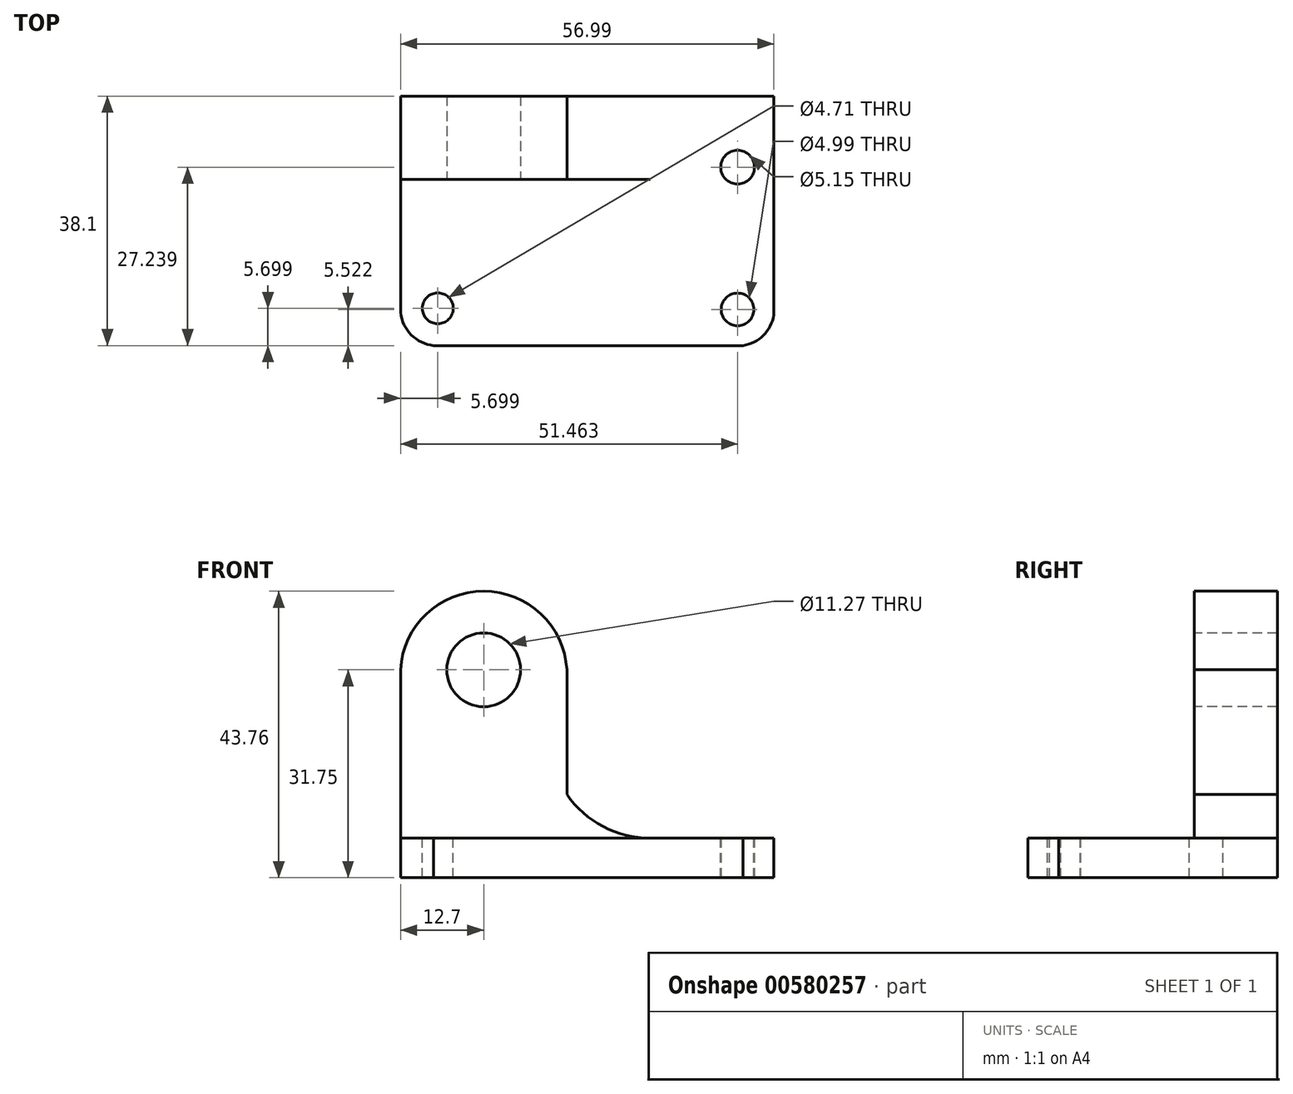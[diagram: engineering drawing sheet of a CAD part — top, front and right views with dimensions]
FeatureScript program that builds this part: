
annotation { "Feature Type Name" : "Feature", "Feature Type Description" : "" }
export const myFeature = defineFeature(function(context is Context, id is Id, definition is map)
    precondition{}
    {
        {
            var Q0;
            Q0=qCreatedBy(makeId("Front.planeOp"),FACE);
            var sketch = newSketch(context, id + "F0", { "sketchPlane" : qUnion([Q0])});
            skLineSegment(sketch, "E0", {"start": v(0, 0) * mm, "end": v(0, 6.04) * mm});
            skLineSegment(sketch, "E1", {"start": v(0, 6.04) * mm, "end": v(56.99, 6.04) * mm});
            skLineSegment(sketch, "E2", {"start": v(56.99, 6.04) * mm, "end": v(56.99, 0) * mm});
            skLineSegment(sketch, "E3", {"start": v(56.99, 0) * mm, "end": v(0, 0) * mm});
            skSolve(sketch);
        }
        {
            var Q0;
            Q0=makeQuery(id+"F0.imprint","IMPRINT",FACE,{"disambiguationData":[TD([[makeQuery(id+"F0.imprint","IMPRINT",EDGE,{"derivedFrom":sQuery(id+"F0.wireOp",EDGE,"E0")}),-1.0]])]});
            extrude(context, id + "F1", {"entities" : qUnion([Q0]), "depth" : 38.1 * mm, "offsetDistance" : 25.4 * mm});
        }
        {
            var Q0;
            Q0=qCreatedBy(makeId("Front.planeOp"),FACE);
            var sketch = newSketch(context, id + "F2", { "sketchPlane" : qUnion([Q0])});
            skLineSegment(sketch, "E4", {"start": v(0, 0) * mm, "end": v(0, 44.45) * mm});
            skLineSegment(sketch, "E5", {"start": v(0, 44.45) * mm, "end": v(25.4, 44.45) * mm});
            skLineSegment(sketch, "E6", {"start": v(25.4, 44.45) * mm, "end": v(25.4, 12.7) * mm});
            skLineSegment(sketch, "E7", {"start": v(25.4, 12.7) * mm, "end": v(38.1, 12.7) * mm});
            skLineSegment(sketch, "E8", {"start": v(38.1, 12.7) * mm, "end": v(38.1, 0) * mm});
            skLineSegment(sketch, "E9", {"start": v(38.1, 0) * mm, "end": v(0, 0) * mm});
            skSolve(sketch);
        }
        {
            var Q0;
            Q0=makeQuery(id+"F2.imprint","IMPRINT",FACE,{"disambiguationData":[TD([[makeQuery(id+"F2.imprint","IMPRINT",EDGE,{"derivedFrom":sQuery(id+"F2.wireOp",EDGE,"E4")}),-1.0]])]});
            extrude(context, id + "F3", {"entities" : qUnion([Q0]), "operationType" : NewBodyOperationType.ADD, "depth" : 12.7 * mm, "offsetDistance" : 25.4 * mm});
        }
        {
            var Q0;
            Q0=makeQuery(id+"F3.opExtrude","CAP_FACE",FACE,{"disambiguationData":[OSD([sQuery(id+"F2.wireOp",EDGE,"E4"),sQuery(id+"F2.wireOp",EDGE,"E5"),sQuery(id+"F2.wireOp",EDGE,"E6"),sQuery(id+"F2.wireOp",EDGE,"E7"),sQuery(id+"F2.wireOp",EDGE,"E8"),sQuery(id+"F2.wireOp",EDGE,"E9")])],"isStart":false});
            var sketch = newSketch(context, id + "F4", { "sketchPlane" : qUnion([Q0])});
            skCircle(sketch, "E10", {"center": v(12.7, 31.75) * mm, "radius": 5.63 * mm});
            skArc(sketch, "E11", {"start": v(25.4, 31.75) * mm, "mid": v(12.7, 43.76) * mm, "end": v(0, 31.75) * mm});
            skArc(sketch, "E12", {"start": v(25.4, 12.7) * mm, "mid": v(30.93, 7.8) * mm, "end": v(38.1, 6.04) * mm});
            skSolve(sketch);
        }
        {
            var Q0;
            {var subQ0=sQuery(id+"F4.wireOp",EDGE,"E11");Q0=makeQuery(id+"F4.imprint","IMPRINT",FACE,{"disambiguationData":[TD([[makeQuery(id+"F4.imprint","IMPRINT",EDGE,{"derivedFrom":subQ0}),-1.0]])]});}
            var Q1;
            Q1=makeQuery(id+"F4.imprint","IMPRINT",FACE,{"disambiguationData":[TD([[makeQuery(id+"F4.imprint","IMPRINT",EDGE,{"derivedFrom":sQuery(id+"F4.wireOp",EDGE,"E10")}),1.0]])]});
            var Q2;
            Q2=makeQuery(id+"F4.imprint","IMPRINT",FACE,{"disambiguationData":[TD([[makeQuery(id+"F4.imprint","IMPRINT",EDGE,{"derivedFrom":sQuery(id+"F4.wireOp",EDGE,"E12")}),1.0]])]});
            extrude(context, id + "F5", {"entities" : qUnion([Q0, Q1, Q2]), "operationType" : NewBodyOperationType.REMOVE, "oppositeDirection" : true, "depth" : 25.4 * mm, "offsetDistance" : 25.4 * mm});
        }
        {
            var Q0;
            Q0=makeQuery(id+"F1.opExtrude","SWEPT_FACE",FACE,{"disambiguationData":[OSD([sQuery(id+"F0.wireOp",EDGE,"E1")])]});
            var sketch = newSketch(context, id + "F6", { "sketchPlane" : qUnion([Q0])});
            skArc(sketch, "E13", {"start": v(0, -31.75) * mm, "mid": v(1.64, -36.46) * mm, "end": v(6.35, -38.1) * mm});
            skArc(sketch, "E14", {"start": v(50.64, -38.1) * mm, "mid": v(55.41, -36.53) * mm, "end": v(56.99, -31.75) * mm});
            skCircle(sketch, "E15", {"center": v(5.7, -32.4) * mm, "radius": 2.36 * mm});
            skCircle(sketch, "E16", {"center": v(51.46, -32.58) * mm, "radius": 2.5 * mm});
            skCircle(sketch, "E17", {"center": v(51.46, -10.86) * mm, "radius": 2.58 * mm});
            skSolve(sketch);
        }
        {
            var Q0;
            {var subQ0=sQuery(id+"F6.wireOp",EDGE,"E14");var subQ1=sQuery(id+"F0.wireOp",EDGE,"E1");var subQ2=makeQuery(id+"F1.opExtrude","CAP_EDGE",EDGE,{"disambiguationData":[OSD([subQ1])],"isStart":false});var subQ3=makeQuery(id+"F6.imprint","INTERSECT",VERTEX,{"disambiguationData":[OD(1.0)],"derivedFrom":[subQ2,subQ0]});Q0=makeQuery(id+"F6.imprint","IMPRINT",FACE,{"disambiguationData":[TD([[makeQuery(id+"F6.imprint","IMPRINT",EDGE,{"disambiguationData":[TD([[subQ3,-1.0]])],"derivedFrom":subQ0}),-1.0]])]});}
            var Q1;
            {var subQ0=sQuery(id+"F6.wireOp",EDGE,"E13");var subQ1=sQuery(id+"F0.wireOp",EDGE,"E1");var subQ4=makeQuery(id+"F1.opExtrude","CAP_EDGE",EDGE,{"disambiguationData":[OSD([subQ1])],"isStart":false});var subQ5=makeQuery(id+"F6.imprint","INTERSECT",VERTEX,{"disambiguationData":[OD(1.0)],"derivedFrom":[subQ4,subQ0]});Q1=makeQuery(id+"F6.imprint","IMPRINT",FACE,{"disambiguationData":[TD([[makeQuery(id+"F6.imprint","IMPRINT",EDGE,{"disambiguationData":[TD([[subQ5,1.0]])],"derivedFrom":subQ0}),-1.0]])]});}
            var Q2;
            Q2=makeQuery(id+"F6.imprint","IMPRINT",FACE,{"disambiguationData":[TD([[makeQuery(id+"F6.imprint","IMPRINT",EDGE,{"derivedFrom":sQuery(id+"F6.wireOp",EDGE,"E17")}),1.0]])]});
            var Q3;
            Q3=makeQuery(id+"F6.imprint","IMPRINT",FACE,{"disambiguationData":[TD([[makeQuery(id+"F6.imprint","IMPRINT",EDGE,{"derivedFrom":sQuery(id+"F6.wireOp",EDGE,"E16")}),1.0]])]});
            var Q4;
            Q4=makeQuery(id+"F6.imprint","IMPRINT",FACE,{"disambiguationData":[TD([[makeQuery(id+"F6.imprint","IMPRINT",EDGE,{"derivedFrom":sQuery(id+"F6.wireOp",EDGE,"E15")}),1.0]])]});
            extrude(context, id + "F7", {"entities" : qUnion([Q0, Q1, Q2, Q3, Q4]), "operationType" : NewBodyOperationType.REMOVE, "oppositeDirection" : true, "depth" : 25.4 * mm, "offsetDistance" : 25.4 * mm});
        }
    });
